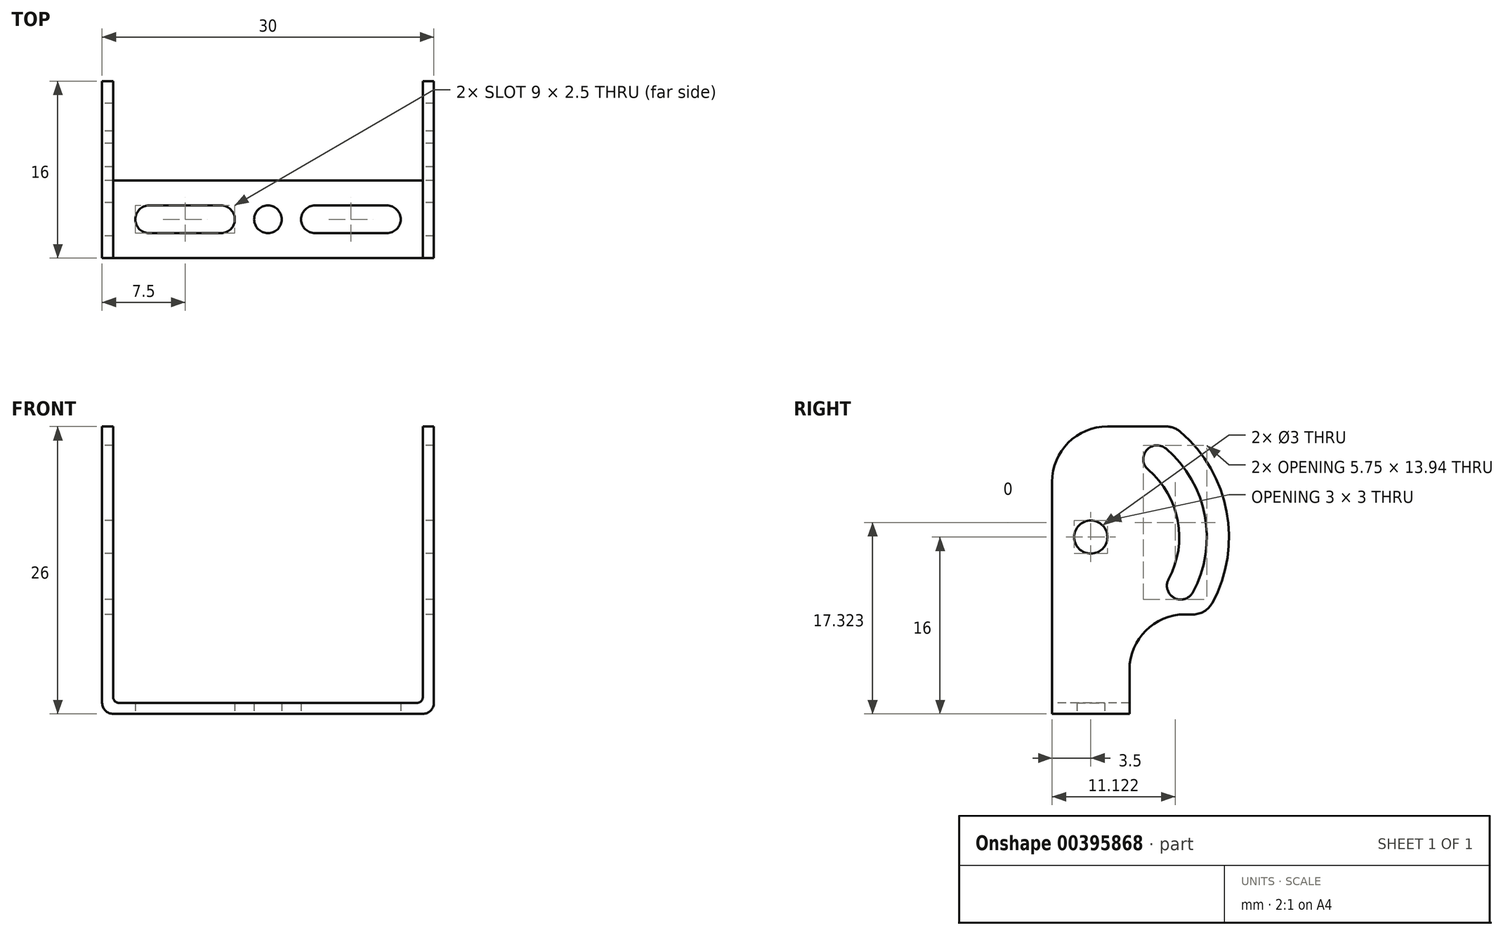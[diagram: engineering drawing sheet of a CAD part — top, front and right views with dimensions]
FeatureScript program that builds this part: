
annotation { "Feature Type Name" : "Feature", "Feature Type Description" : "" }
export const myFeature = defineFeature(function(context is Context, id is Id, definition is map)
    precondition{}
    {
        {
            var Q0;
            Q0=qCreatedBy(makeId("Right.planeOp"),FACE);
            var sketch = newSketch(context, id + "F0", { "sketchPlane" : qUnion([Q0])});
            skLineSegment(sketch, "E0.bottom", {"start": v(-3.5, 0) * mm, "end": v(3.5, 0) * mm});
            skLineSegment(sketch, "E0.top", {"start": v(1.5, 26) * mm, "end": v(6.8, 26) * mm});
            skLineSegment(sketch, "E0.left", {"start": v(-3.5, 0) * mm, "end": v(-3.5, 21) * mm});
            skCircle(sketch, "E1", {"center": v(0, 16) * mm, "radius": 1.5 * mm});
            skPoint(sketch, "E2.visualSharp", {"position": v(-3.5, 26) * mm});
            skArc(sketch, "E2.filletArc", {"start": v(1.5, 26) * mm, "mid": v(-2.04, 24.54) * mm, "end": v(-3.5, 21) * mm});
            skArc(sketch, "E3", {"start": v(11, 10.05) * mm, "mid": v(12.29, 18.3) * mm, "end": v(8.1, 25.52) * mm});
            skLineSegment(sketch, "E4", {"start": v(9.23, 9) * mm, "end": v(8.5, 9) * mm});
            skLineSegment(sketch, "E5", {"start": v(3.5, 4) * mm, "end": v(3.5, 0) * mm});
            skPoint(sketch, "E6.visualSharp", {"position": v(7.5, 26) * mm});
            skArc(sketch, "E6.filletArc", {"start": v(8.1, 25.52) * mm, "mid": v(7.5, 25.88) * mm, "end": v(6.8, 26) * mm});
            skPoint(sketch, "E7.visualSharp", {"position": v(10.36, 9) * mm});
            skArc(sketch, "E7.filletArc", {"start": v(9.23, 9) * mm, "mid": v(10.26, 9.28) * mm, "end": v(11, 10.05) * mm});
            skPoint(sketch, "E8.visualSharp", {"position": v(3.5, 9) * mm});
            skArc(sketch, "E8.filletArc", {"start": v(8.5, 9) * mm, "mid": v(4.96, 7.54) * mm, "end": v(3.5, 4) * mm});
            skArc(sketch, "E9.0", {"start": v(9.23, 11) * mm, "mid": v(10.32, 17.93) * mm, "end": v(6.8, 24) * mm});
            skArc(sketch, "E10.0", {"start": v(7.03, 12.2) * mm, "mid": v(7.86, 17.47) * mm, "end": v(5.18, 22.1) * mm});
            skArc(sketch, "E11", {"start": v(6.8, 24) * mm, "mid": v(5.04, 23.86) * mm, "end": v(5.18, 22.1) * mm});
            skArc(sketch, "E12", {"start": v(7.03, 12.2) * mm, "mid": v(7.54, 10.5) * mm, "end": v(9.23, 11) * mm});
            skLineSegment(sketch, "E13", {"start": v(7.03, 12.2) * mm, "end": v(9.23, 11) * mm, "construction": true});
            skLineSegment(sketch, "E14", {"start": v(6.8, 24) * mm, "end": v(5.18, 22.1) * mm, "construction": true});
            skLineSegment(sketch, "E15", {"start": v(0, 16) * mm, "end": v(7.03, 12.2) * mm, "construction": true});
            skLineSegment(sketch, "E16", {"start": v(0, 16) * mm, "end": v(5.18, 22.1) * mm, "construction": true});
            skSolve(sketch);
        }
        {
            var Q0;
            Q0=qSketchRegion(id+"F0",true);
            extrude(context, id + "F1", {"entities" : qUnion([Q0]), "endBound" : BoundingType.SYMMETRIC, "depth" : 30 * mm});
        }
        {
            var Q0;
            Q0=makeQuery(id+"F1.opExtrude","SWEPT_FACE",FACE,{"disambiguationData":[OSD([sQuery(id+"F0.wireOp",EDGE,"E0.left")])]});
            var sketch = newSketch(context, id + "F2", { "sketchPlane" : qUnion([Q0])});
            skLineSegment(sketch, "E17.bottom", {"start": v(-14, 26) * mm, "end": v(14, 26) * mm});
            skLineSegment(sketch, "E17.top", {"start": v(-13.5, 1) * mm, "end": v(13.5, 1) * mm});
            skLineSegment(sketch, "E17.left", {"start": v(-14, 26) * mm, "end": v(-14, 1.5) * mm});
            skLineSegment(sketch, "E17.right", {"start": v(14, 26) * mm, "end": v(14, 1.5) * mm});
            skPoint(sketch, "E18.visualSharp", {"position": v(-14, 1) * mm});
            skArc(sketch, "E18.filletArc", {"start": v(-14, 1.5) * mm, "mid": v(-13.85, 1.15) * mm, "end": v(-13.5, 1) * mm});
            skPoint(sketch, "E19.visualSharp", {"position": v(14, 1) * mm});
            skArc(sketch, "E19.filletArc", {"start": v(13.5, 1) * mm, "mid": v(13.85, 1.15) * mm, "end": v(14, 1.5) * mm});
            skSolve(sketch);
        }
        {
            var Q0;
            Q0=qSketchRegion(id+"F2",true);
            extrude(context, id + "F3", {"entities" : qUnion([Q0]), "operationType" : NewBodyOperationType.REMOVE, "oppositeDirection" : true, "depth" : 25 * mm});
        }
        {
            var Q0;
            Q0=makeQuery(id+"F1.opExtrude","CAP_EDGE",EDGE,{"disambiguationData":[OSD([sQuery(id+"F0.wireOp",EDGE,"E0.bottom")])],"isStart":true});
            var Q1;
            Q1=makeQuery(id+"F1.opExtrude","CAP_EDGE",EDGE,{"disambiguationData":[OSD([sQuery(id+"F0.wireOp",EDGE,"E0.bottom")])],"isStart":false});
            fillet(context, id + "F4", {"entities" : qUnion([Q0, Q1]), "radius" : 1 * mm, "tangentPropagation" : true, "allowEdgeOverflow" : false});
        }
        {
            var Q0;
            Q0=makeQuery(id+"F1.opExtrude","SWEPT_FACE",FACE,{"disambiguationData":[OSD([sQuery(id+"F0.wireOp",EDGE,"E0.bottom")])]});
            var sketch = newSketch(context, id + "F5", { "sketchPlane" : qUnion([Q0])});
            skCircle(sketch, "E20", {"center": v(0, 0) * mm, "radius": 1.25 * mm});
            skLineSegment(sketch, "E21", {"start": v(-10.75, 0) * mm, "end": v(-4.25, 0) * mm, "construction": true});
            skArc(sketch, "E22.0.startCap", {"start": v(-10.75, -1.25) * mm, "mid": v(-12, 0) * mm, "end": v(-10.75, 1.25) * mm});
            skArc(sketch, "E22.0.endCap", {"start": v(-4.25, 1.25) * mm, "mid": v(-3, 0) * mm, "end": v(-4.25, -1.25) * mm});
            skLineSegment(sketch, "E22.0.left", {"start": v(-10.75, 1.25) * mm, "end": v(-4.25, 1.25) * mm});
            skLineSegment(sketch, "E22.0.right", {"start": v(-10.75, -1.25) * mm, "end": v(-4.25, -1.25) * mm});
            skLineSegment(sketch, "E23.MirrorCS", {"start": v(10.75, 1.25) * mm, "end": v(4.25, 1.25) * mm});
            skArc(sketch, "E24.MirrorCS", {"start": v(4.25, 1.25) * mm, "mid": v(3, 0) * mm, "end": v(4.25, -1.25) * mm});
            skLineSegment(sketch, "E25.MirrorCS", {"start": v(10.75, -1.25) * mm, "end": v(4.25, -1.25) * mm});
            skArc(sketch, "E26.MirrorCS", {"start": v(10.75, -1.25) * mm, "mid": v(12, 0) * mm, "end": v(10.75, 1.25) * mm});
            skSolve(sketch);
        }
        {
            var Q0;
            Q0=qSketchRegion(id+"F5",true);
            extrude(context, id + "F6", {"entities" : qUnion([Q0]), "operationType" : NewBodyOperationType.REMOVE, "oppositeDirection" : true, "depth" : 25 * mm});
        }
    });
